# Revit family: ledpanelrc-mo_sq595-35w-ble-4000-wh-u19_542003015700
name_source: partatom
category: Leuchten
revit_build: Autodesk Revit 2016 (Build: 20190508_0715(x64)
units: mm (PartAtom-declared; Revit-internal decimal feet)

## family parameters
Basisbauteil = Fläche
Beim Laden mit Abzugskörper schneiden = Nein
Bemaßung runder Anschluss = Durchmesser verwenden
Gemeinsam genutzt = Nein
Lichtquelle = Nein
Raumberechnungspunkt = Nein
Teiletyp = Normal

## types (1)
- LEDPanelRc-Mo Sq595-35W-BLE-4000-WH-U19 (1 x LED, 4270 lm)
    Approval mark = CE, ENEC
    Beschreibung = Architectural LED panel with direct/indirect light. Unique low glare optics. Suitable for office applications, UGR<19. Perfect replacement of traditional CFL 55W panels – offering up to 50% energy saving.
    CIE Flux Codes = 60 86 97 100 100
    Control Gear = Electronic ballast
    Height = 0 mm  [stored 0 ft]
    Hersteller = OPPLE
    Lamp Light Flux = 4270 lm
    Lamp count = 1
    Lampe = 1 x LED
    Length = 595 mm
    Luminous efficacy = 122 lm/W
    ModVariant = Nein
    Modell = 542003015700
    Mounting Place = Ceiling
    Mounting Type = Recessed
    Number of Poles = 1
    OnlyDefault = Ja
    Power Factor = 1
    Product Name = LEDPanelRc-Mo Sq595-35W-BLE-4000-WH-U19
    Product group = Panel Monza
    ProductGroupID = 411
    Protection Class = Protection class II
    Protection Degree = IP 20
    RLX_Detail_Level = 1
    RlxData = <blob elided: 78133 chars, md5=26382699>
    Scheinlast = 35 VA
    Socket = socket
    Standby Power = 0 W
    System Light Flux = 4270 lm
    System Power = 35 W
    Typenbild = 542003015700.jpg
    Typenkommentare = Product without accessories
    URL = http://relux.com
    VarID = ---
    Voltage = 0 V
    Vorgabe-Ansicht = 1800 mm
    Weight = 0.00 kg
    Width = 595 mm

note: [stored X ft] marks values corroborated as IEEE doubles in the binary element streams (Revit-internal decimal feet)

## geometry (parser evidence)
native form markers: Sweep x9
no freeform markers — native parametric forms only
